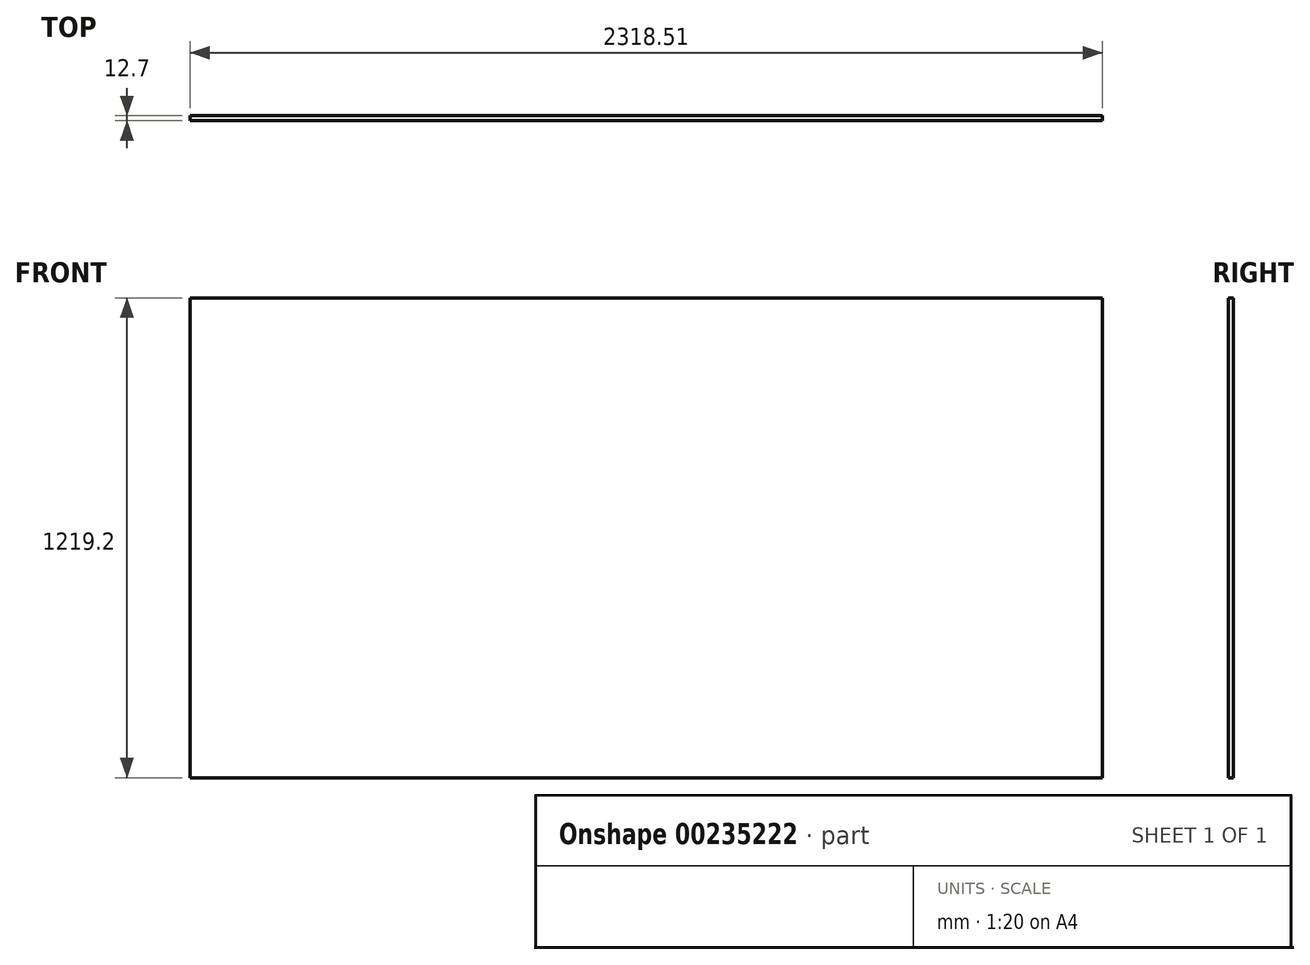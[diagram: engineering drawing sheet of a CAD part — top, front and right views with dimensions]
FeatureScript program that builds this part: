
annotation { "Feature Type Name" : "Feature", "Feature Type Description" : "" }
export const myFeature = defineFeature(function(context is Context, id is Id, definition is map)
    precondition{}
    {
        {
            var Q0;
            Q0=qCreatedBy(makeId("Front.planeOp"),FACE);
            var sketch = newSketch(context, id + "F0", { "sketchPlane" : qUnion([Q0])});
            skLineSegment(sketch, "E0.bottom", {"start": v(0, 0) * mm, "end": v(2318.51, 0) * mm});
            skLineSegment(sketch, "E0.top", {"start": v(0, 1219.2) * mm, "end": v(2318.51, 1219.2) * mm});
            skLineSegment(sketch, "E0.left", {"start": v(0, 0) * mm, "end": v(0, 1219.2) * mm});
            skLineSegment(sketch, "E0.right", {"start": v(2318.51, 0) * mm, "end": v(2318.51, 1219.2) * mm});
            skSolve(sketch);
        }
        {
            var Q0;
            Q0=makeQuery(id+"F0.imprint","IMPRINT",FACE,{"disambiguationData":[TD([[makeQuery(id+"F0.imprint","IMPRINT",EDGE,{"derivedFrom":sQuery(id+"F0.wireOp",EDGE,"E0.bottom")}),1.0]])]});
            extrude(context, id + "F1", {"entities" : qUnion([Q0]), "depth" : 12.7 * mm});
        }
    });
